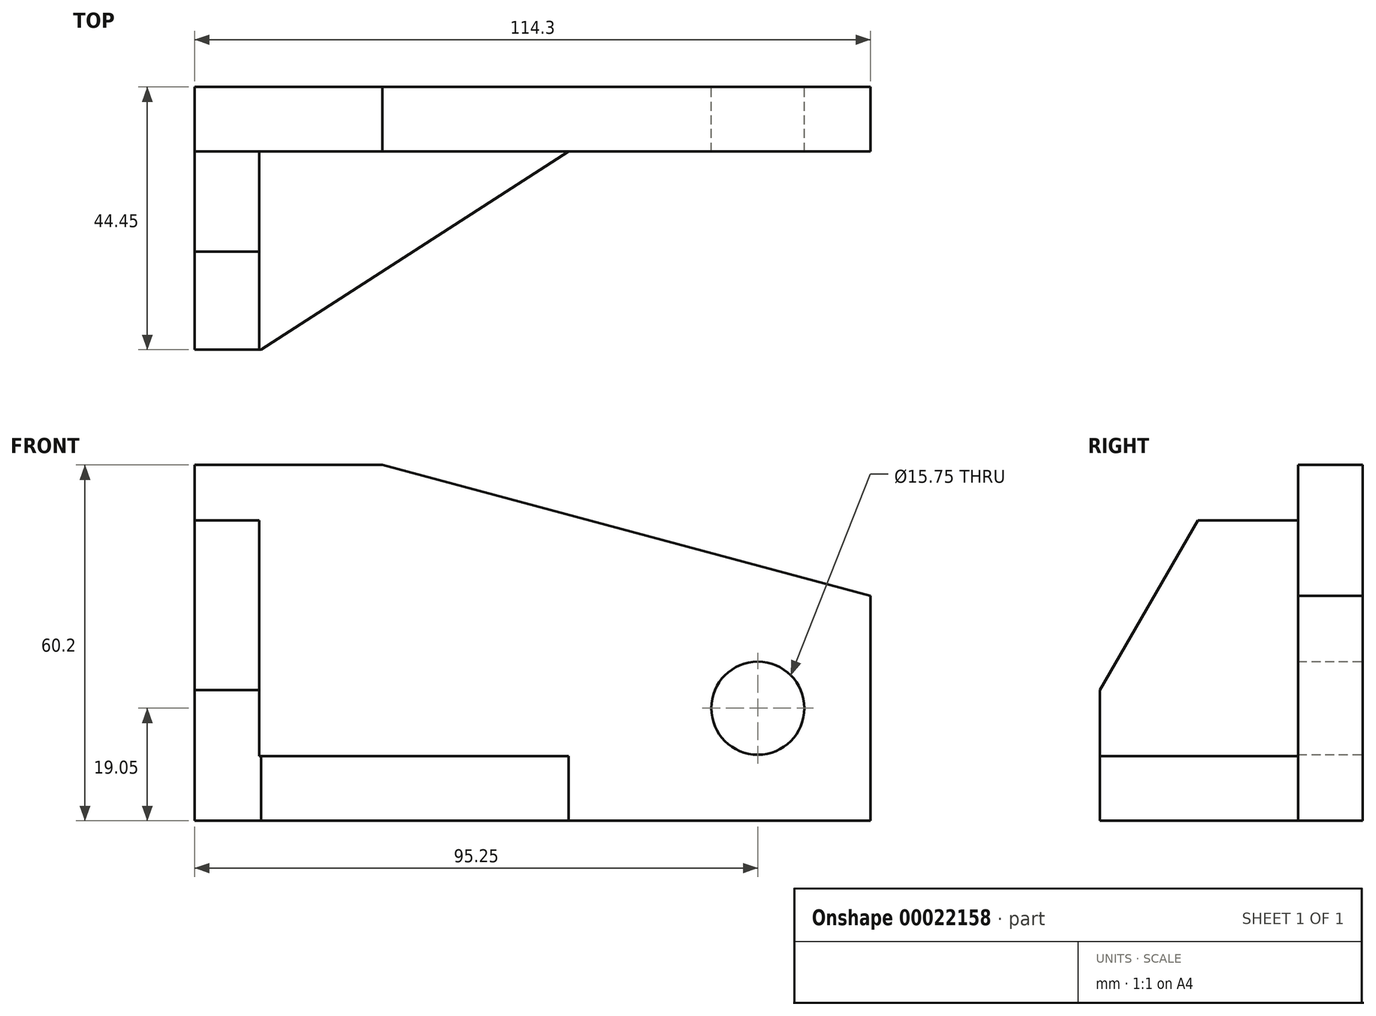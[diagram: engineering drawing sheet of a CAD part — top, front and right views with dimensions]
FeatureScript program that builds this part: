
annotation { "Feature Type Name" : "Feature", "Feature Type Description" : "" }
export const myFeature = defineFeature(function(context is Context, id is Id, definition is map)
    precondition{}
    {
        {
            var Q0;
            Q0=qCreatedBy(makeId("Front.planeOp"),FACE);
            var sketch = newSketch(context, id + "F0", { "sketchPlane" : qUnion([Q0])});
            skLineSegment(sketch, "E0.bottom", {"start": v(0, 0) * mm, "end": v(114.3, 0) * mm});
            skLineSegment(sketch, "E0.top", {"start": v(0, 60.2) * mm, "end": v(31.75, 60.2) * mm});
            skLineSegment(sketch, "E0.left", {"start": v(0, 0) * mm, "end": v(0, 60.2) * mm});
            skLineSegment(sketch, "E0.right", {"start": v(114.3, 0) * mm, "end": v(114.3, 38.08) * mm});
            skLineSegment(sketch, "E1", {"start": v(31.75, 60.2) * mm, "end": v(114.3, 38.08) * mm});
            skCircle(sketch, "E2", {"center": v(95.25, 19.05) * mm, "radius": 7.87 * mm});
            skSolve(sketch);
        }
        {
            var Q0;
            Q0 = qSketchRegion(id + "F0", true);
            extrude(context, id + "F1", {"entities" : qUnion([Q0]), "depth" : 10.92 * mm});
        }
        {
            var Q0;
            Q0=qCreatedBy(makeId("Right.planeOp"),FACE);
            var sketch = newSketch(context, id + "F2", { "sketchPlane" : qUnion([Q0])});
            skLineSegment(sketch, "E3.bottom", {"start": v(0, 0) * mm, "end": v(-44.45, 0) * mm});
            skLineSegment(sketch, "E3.top", {"start": v(0, 50.8) * mm, "end": v(-27.88, 50.8) * mm});
            skLineSegment(sketch, "E3.left", {"start": v(0, 0) * mm, "end": v(0, 50.8) * mm});
            skLineSegment(sketch, "E3.right", {"start": v(-44.45, 0) * mm, "end": v(-44.45, 22.1) * mm});
            skLineSegment(sketch, "E4", {"start": v(-44.45, 22.1) * mm, "end": v(-27.88, 50.8) * mm});
            skSolve(sketch);
        }
        {
            var Q0;
            Q0 = qSketchRegion(id + "F2", true);
            extrude(context, id + "F3", {"entities" : qUnion([Q0]), "operationType" : NewBodyOperationType.ADD, "depth" : 10.92 * mm});
        }
        {
            var Q0;
            Q0=qCreatedBy(makeId("Top.planeOp"),FACE);
            var sketch = newSketch(context, id + "F4", { "sketchPlane" : qUnion([Q0])});
            skLineSegment(sketch, "E5.bottom", {"start": v(0, 0) * mm, "end": v(63.5, 0) * mm});
            skLineSegment(sketch, "E5.top", {"start": v(0, -44.45) * mm, "end": v(11.21, -44.45) * mm});
            skLineSegment(sketch, "E5.left", {"start": v(0, 0) * mm, "end": v(0, -44.45) * mm});
            skLineSegment(sketch, "E5.right", {"start": v(63.5, 0) * mm, "end": v(63.5, -10.75) * mm});
            skLineSegment(sketch, "E6", {"start": v(63.5, -10.75) * mm, "end": v(11.21, -44.45) * mm});
            skSolve(sketch);
        }
        {
            var Q0;
            Q0 = qSketchRegion(id + "F4", true);
            extrude(context, id + "F5", {"entities" : qUnion([Q0]), "operationType" : NewBodyOperationType.ADD, "depth" : 10.92 * mm});
        }
    });
